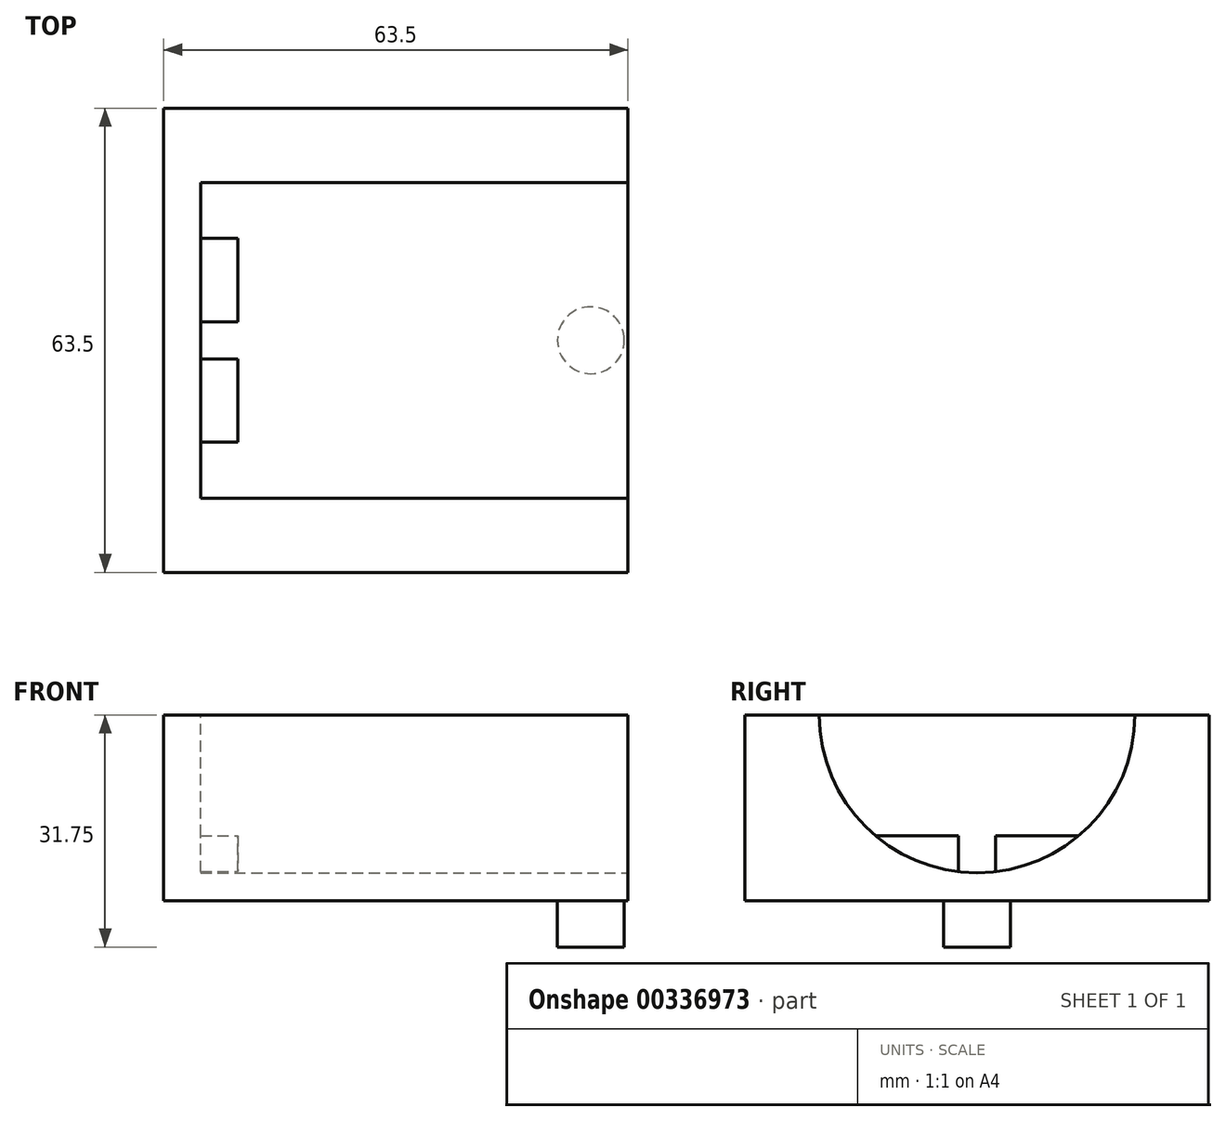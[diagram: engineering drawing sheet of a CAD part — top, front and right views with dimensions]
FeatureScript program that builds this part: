
annotation { "Feature Type Name" : "Feature", "Feature Type Description" : "" }
export const myFeature = defineFeature(function(context is Context, id is Id, definition is map)
    precondition{}
    {
        {
            var Q0;
            Q0=qCreatedBy(makeId("Top.planeOp"),FACE);
            var sketch = newSketch(context, id + "F0", { "sketchPlane" : qUnion([Q0])});
            skLineSegment(sketch, "E0.bottom", {"start": v(31.75, 31.75) * mm, "end": v(-31.75, 31.75) * mm});
            skLineSegment(sketch, "E0.top", {"start": v(31.75, -31.75) * mm, "end": v(-31.75, -31.75) * mm});
            skLineSegment(sketch, "E0.left", {"start": v(31.75, 31.75) * mm, "end": v(31.75, -31.75) * mm});
            skLineSegment(sketch, "E0.right", {"start": v(-31.75, 31.75) * mm, "end": v(-31.75, -31.75) * mm});
            skPoint(sketch, "E0.middle", {"position": v(0, 0) * mm});
            skSolve(sketch);
        }
        {
            var Q0;
            Q0 = qSketchRegion(id + "F0", true);
            extrude(context, id + "F1", {"entities" : qUnion([Q0]), "depth" : 25.4 * mm});
        }
        {
            var Q0;
            Q0=makeQuery(id+"F1.opExtrude","SWEPT_FACE",FACE,{"disambiguationData":[OSD([sQuery(id+"F0.wireOp",EDGE,"E0.left")])]});
            var sketch = newSketch(context, id + "F2", { "sketchPlane" : qUnion([Q0])});
            skCircle(sketch, "E1", {"center": v(0, 25.4) * mm, "radius": 21.59 * mm});
            skSolve(sketch);
        }
        {
            var Q0;
            Q0 = qSketchRegion(id + "F2", true);
            extrude(context, id + "F3", {"entities" : qUnion([Q0]), "operationType" : NewBodyOperationType.REMOVE, "oppositeDirection" : true, "depth" : 53.34 * mm});
        }
        {
            var Q0;
            Q0=makeQuery(id+"F1.opExtrude","CAP_FACE",FACE,{"disambiguationData":[OSD([sQuery(id+"F0.wireOp",EDGE,"E0.bottom"),sQuery(id+"F0.wireOp",EDGE,"E0.top"),sQuery(id+"F0.wireOp",EDGE,"E0.left"),sQuery(id+"F0.wireOp",EDGE,"E0.right")])],"isStart":true});
            var sketch = newSketch(context, id + "F4", { "sketchPlane" : qUnion([Q0])});
            skCircle(sketch, "E2", {"center": v(26.67, 0) * mm, "radius": 4.57 * mm});
            skSolve(sketch);
        }
        {
            var Q0;
            Q0 = qSketchRegion(id + "F4", true);
            extrude(context, id + "F5", {"entities" : qUnion([Q0]), "operationType" : NewBodyOperationType.ADD, "depth" : 6.35 * mm});
        }
        {
            var Q0;
            Q0=makeQuery(id+"F3.boolean.opBoolean","COPY",FACE,{"derivedFrom":makeQuery(id+"F3.opExtrude","CAP_FACE",FACE,{"disambiguationData":[OSD([sQuery(id+"F2.wireOp",EDGE,"E1")])],"isStart":false})});
            var sketch = newSketch(context, id + "F6", { "sketchPlane" : qUnion([Q0])});
            skLineSegment(sketch, "E3", {"start": v(-2.54, 3.96) * mm, "end": v(-2.54, 8.9) * mm});
            skLineSegment(sketch, "E4", {"start": v(2.54, 8.9) * mm, "end": v(2.54, 3.96) * mm});
            skLineSegment(sketch, "E5", {"start": v(-13.91, 8.9) * mm, "end": v(-2.54, 8.9) * mm});
            skArc(sketch, "E6", {"start": v(-2.54, 3.96) * mm, "mid": v(0, 3.8) * mm, "end": v(2.54, 3.96) * mm});
            skArc(sketch, "E7.trimOffspring", {"start": v(13.91, 8.9) * mm, "mid": v(0, 47) * mm, "end": v(-13.91, 8.9) * mm});
            skLineSegment(sketch, "E8.trimOffspring", {"start": v(2.54, 8.9) * mm, "end": v(13.91, 8.9) * mm});
            skSolve(sketch);
        }
        {
            var Q0;
            Q0 = qSketchRegion(id + "F6", true);
            extrude(context, id + "F7", {"entities" : qUnion([Q0]), "operationType" : NewBodyOperationType.REMOVE, "oppositeDirection" : true, "depth" : 5.08 * mm});
        }
        {
            var Q0;
            Q0 = qSketchRegion(id + "F6", true);
            extrude(context, id + "F8", {"entities" : qUnion([Q0]), "operationType" : NewBodyOperationType.REMOVE, "oppositeDirection" : true, "depth" : 5.08 * mm});
        }
    });
